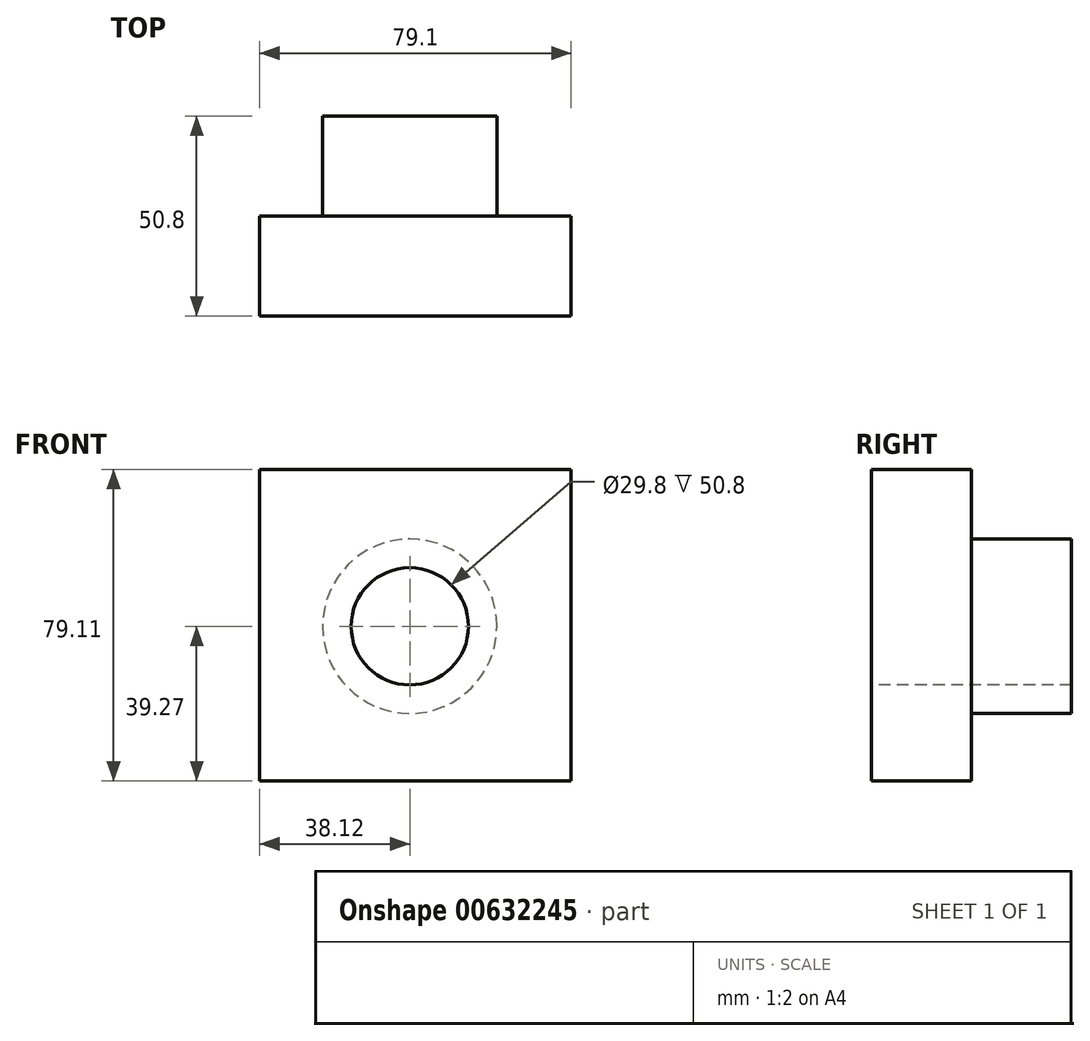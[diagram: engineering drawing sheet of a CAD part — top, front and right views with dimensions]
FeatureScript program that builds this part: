
annotation { "Feature Type Name" : "Feature", "Feature Type Description" : "" }
export const myFeature = defineFeature(function(context is Context, id is Id, definition is map)
    precondition{}
    {
        {
            var Q0;
            Q0=qCreatedBy(makeId("Front.planeOp"),FACE);
            var sketch = newSketch(context, id + "F0", { "sketchPlane" : qUnion([Q0])});
            skLineSegment(sketch, "E0.bottom", {"start": v(-38.12, 39.84) * mm, "end": v(40.98, 39.84) * mm});
            skLineSegment(sketch, "E0.top", {"start": v(-38.12, -39.27) * mm, "end": v(40.98, -39.27) * mm});
            skLineSegment(sketch, "E0.left", {"start": v(-38.12, 39.84) * mm, "end": v(-38.12, -39.27) * mm});
            skLineSegment(sketch, "E0.right", {"start": v(40.98, 39.84) * mm, "end": v(40.98, -39.27) * mm});
            skCircle(sketch, "E1", {"center": v(0, 0) * mm, "radius": 22.16 * mm});
            skCircle(sketch, "E2", {"center": v(0, 0) * mm, "radius": 14.9 * mm});
            skSolve(sketch);
        }
        {
            var Q0;
            Q0=makeQuery(id+"F0.imprint","IMPRINT",FACE,{"disambiguationData":[TD([[makeQuery(id+"F0.imprint","IMPRINT",EDGE,{"derivedFrom":sQuery(id+"F0.wireOp",EDGE,"E0.bottom")}),-1.0]])]});
            var Q1;
            Q1=makeQuery(id+"F0.imprint","IMPRINT",FACE,{"disambiguationData":[TD([[makeQuery(id+"F0.imprint","IMPRINT",EDGE,{"derivedFrom":sQuery(id+"F0.wireOp",EDGE,"E2")}),1.0]])]});
            var Q2;
            Q2=makeQuery(id+"F0.imprint","IMPRINT",FACE,{"disambiguationData":[TD([[makeQuery(id+"F0.imprint","IMPRINT",EDGE,{"derivedFrom":sQuery(id+"F0.wireOp",EDGE,"E1")}),1.0]])]});
            extrude(context, id + "F1", {"entities" : qUnion([Q0, Q1, Q2]), "depth" : 25.4 * mm, "offsetDistance" : 25.4 * mm});
        }
        {
            var Q0;
            Q0=makeQuery(id+"F0.imprint","IMPRINT",FACE,{"disambiguationData":[TD([[makeQuery(id+"F0.imprint","IMPRINT",EDGE,{"derivedFrom":sQuery(id+"F0.wireOp",EDGE,"E1")}),1.0]])]});
            extrude(context, id + "F2", {"entities" : qUnion([Q0]), "operationType" : NewBodyOperationType.ADD, "oppositeDirection" : true, "depth" : 25.4 * mm, "offsetDistance" : 25.4 * mm});
        }
        {
            var Q0;
            Q0=makeQuery(id+"F0.imprint","IMPRINT",FACE,{"disambiguationData":[TD([[makeQuery(id+"F0.imprint","IMPRINT",EDGE,{"derivedFrom":sQuery(id+"F0.wireOp",EDGE,"E2")}),1.0]])]});
            extrude(context, id + "F3", {"entities" : qUnion([Q0]), "operationType" : NewBodyOperationType.REMOVE, "endBound" : BoundingType.THROUGH_ALL, "depth" : 25.4 * mm, "offsetDistance" : 25.4 * mm});
        }
    });
